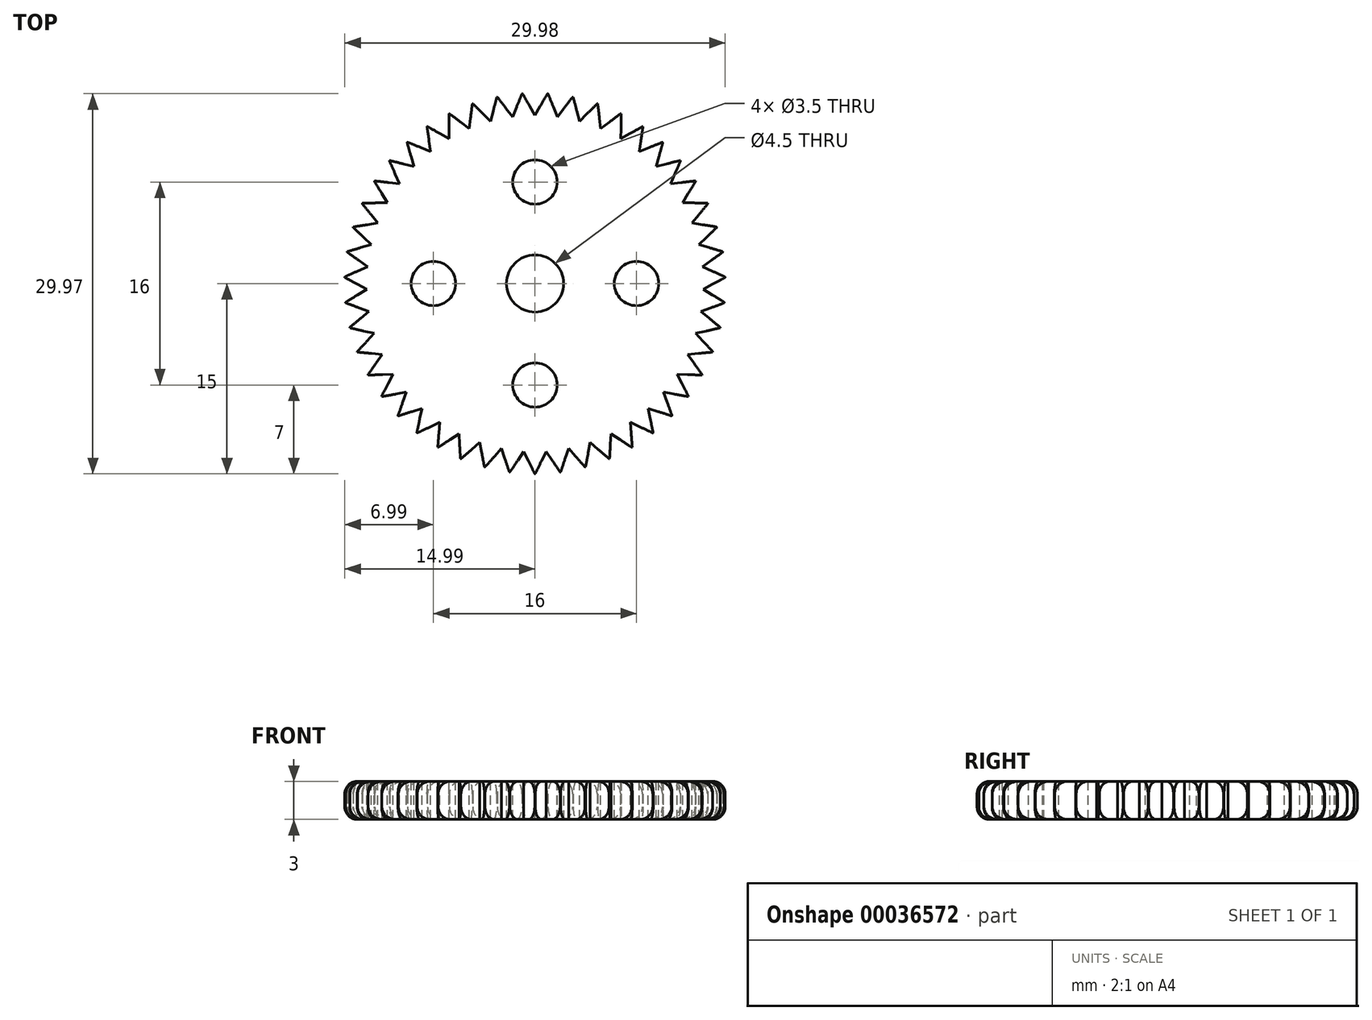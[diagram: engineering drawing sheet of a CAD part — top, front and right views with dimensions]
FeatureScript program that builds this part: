
annotation { "Feature Type Name" : "Feature", "Feature Type Description" : "" }
export const myFeature = defineFeature(function(context is Context, id is Id, definition is map)
    precondition{}
    {
        {
            var Q0;
            Q0=qCreatedBy(makeId("Top.planeOp"),FACE);
            var sketch = newSketch(context, id + "F0", { "sketchPlane" : qUnion([Q0])});
            skCircle(sketch, "E0", {"center": v(0, 0) * mm, "radius": 15 * mm});
            skCircle(sketch, "E1", {"center": v(0, 0) * mm, "radius": 2.25 * mm});
            skSolve(sketch);
        }
        {
            var Q0;
            Q0 = qSketchRegion(id + "F0", true);
            extrude(context, id + "F1", {"entities" : qUnion([Q0]), "depth" : 3 * mm});
        }
        {
            var Q0;
            Q0=makeQuery(id+"F1.opExtrude","CAP_EDGE",EDGE,{"disambiguationData":[OSD([sQuery(id+"F0.wireOp",EDGE,"E0")])],"isStart":false});
            var Q1;
            Q1=makeQuery(id+"F1.opExtrude","CAP_EDGE",EDGE,{"disambiguationData":[OSD([sQuery(id+"F0.wireOp",EDGE,"E0")])],"isStart":true});
            fillet(context, id + "F2", {"entities" : qUnion([Q0, Q1]), "radius" : 1 * mm, "tangentPropagation" : true, "allowEdgeOverflow" : false});
        }
        {
            var Q0;
            Q0=makeQuery(id+"F1.opExtrude","CAP_FACE",FACE,{"disambiguationData":[OSD([sQuery(id+"F0.wireOp",EDGE,"E0"),sQuery(id+"F0.wireOp",EDGE,"E1")])],"isStart":false});
            var sketch = newSketch(context, id + "F3", { "sketchPlane" : qUnion([Q0])});
            skCircle(sketch, "E2.cCircle", {"center": v(0, 14.42) * mm, "radius": 0.58 * mm, "construction": true});
            skLineSegment(sketch, "E2.0", {"start": v(1, 15) * mm, "end": v(0, 13.27) * mm});
            skLineSegment(sketch, "E2.1", {"start": v(0, 13.27) * mm, "end": v(-1, 15) * mm});
            skLineSegment(sketch, "E2.2", {"start": v(-1, 15) * mm, "end": v(1, 15) * mm});
            skPoint(sketch, "E3", {"position": v(0, 15) * mm});
            skLineSegment(sketch, "E4.1.0", {"start": v(-1, 15) * mm, "end": v(-1.77, 13.15) * mm});
            skLineSegment(sketch, "E4.1.1", {"start": v(-1.77, 13.15) * mm, "end": v(-3, 14.73) * mm});
            skLineSegment(sketch, "E4.1.2", {"start": v(-3, 14.73) * mm, "end": v(-1, 15) * mm});
            skLineSegment(sketch, "E4.2.0", {"start": v(-3, 14.73) * mm, "end": v(-3.5, 12.8) * mm});
            skLineSegment(sketch, "E4.2.1", {"start": v(-3.5, 12.8) * mm, "end": v(-4.93, 14.2) * mm});
            skLineSegment(sketch, "E4.2.2", {"start": v(-4.93, 14.2) * mm, "end": v(-3, 14.73) * mm});
            skLineSegment(sketch, "E4.3.0", {"start": v(-4.94, 14.2) * mm, "end": v(-5.18, 12.22) * mm});
            skLineSegment(sketch, "E4.3.1", {"start": v(-5.18, 12.22) * mm, "end": v(-6.78, 13.42) * mm});
            skLineSegment(sketch, "E4.3.2", {"start": v(-6.78, 13.42) * mm, "end": v(-4.94, 14.2) * mm});
            skLineSegment(sketch, "E4.4.0", {"start": v(-6.78, 13.42) * mm, "end": v(-6.76, 11.42) * mm});
            skLineSegment(sketch, "E4.4.1", {"start": v(-6.76, 11.42) * mm, "end": v(-8.5, 12.4) * mm});
            skLineSegment(sketch, "E4.4.2", {"start": v(-8.5, 12.4) * mm, "end": v(-6.78, 13.42) * mm});
            skLineSegment(sketch, "E4.5.0", {"start": v(-8.51, 12.4) * mm, "end": v(-8.22, 10.41) * mm});
            skLineSegment(sketch, "E4.5.1", {"start": v(-8.22, 10.41) * mm, "end": v(-10.08, 11.15) * mm});
            skLineSegment(sketch, "E4.5.2", {"start": v(-10.08, 11.15) * mm, "end": v(-8.51, 12.4) * mm});
            skLineSegment(sketch, "E4.6.0", {"start": v(-10.09, 11.15) * mm, "end": v(-9.54, 9.22) * mm});
            skLineSegment(sketch, "E4.6.1", {"start": v(-9.54, 9.22) * mm, "end": v(-11.48, 9.7) * mm});
            skLineSegment(sketch, "E4.6.2", {"start": v(-11.48, 9.7) * mm, "end": v(-10.09, 11.15) * mm});
            skLineSegment(sketch, "E4.7.0", {"start": v(-11.48, 9.7) * mm, "end": v(-10.68, 7.87) * mm});
            skLineSegment(sketch, "E4.7.1", {"start": v(-10.68, 7.87) * mm, "end": v(-12.67, 8.1) * mm});
            skLineSegment(sketch, "E4.7.2", {"start": v(-12.67, 8.1) * mm, "end": v(-11.48, 9.7) * mm});
            skLineSegment(sketch, "E4.8.0", {"start": v(-12.67, 8.09) * mm, "end": v(-11.64, 6.38) * mm});
            skLineSegment(sketch, "E4.8.1", {"start": v(-11.64, 6.38) * mm, "end": v(-13.63, 6.33) * mm});
            skLineSegment(sketch, "E4.8.2", {"start": v(-13.63, 6.33) * mm, "end": v(-12.67, 8.09) * mm});
            skLineSegment(sketch, "E4.9.0", {"start": v(-13.64, 6.32) * mm, "end": v(-12.38, 4.77) * mm});
            skLineSegment(sketch, "E4.9.1", {"start": v(-12.38, 4.77) * mm, "end": v(-14.36, 4.46) * mm});
            skLineSegment(sketch, "E4.9.2", {"start": v(-14.36, 4.46) * mm, "end": v(-13.64, 6.32) * mm});
            skLineSegment(sketch, "E4.10.0", {"start": v(-14.36, 4.45) * mm, "end": v(-12.9, 3.08) * mm});
            skLineSegment(sketch, "E4.10.1", {"start": v(-12.9, 3.08) * mm, "end": v(-14.82, 2.5) * mm});
            skLineSegment(sketch, "E4.10.2", {"start": v(-14.82, 2.5) * mm, "end": v(-14.36, 4.45) * mm});
            skLineSegment(sketch, "E4.11.0", {"start": v(-14.82, 2.5) * mm, "end": v(-13.2, 1.33) * mm});
            skLineSegment(sketch, "E4.11.1", {"start": v(-13.2, 1.33) * mm, "end": v(-15.02, 0.5) * mm});
            skLineSegment(sketch, "E4.11.2", {"start": v(-15.02, 0.5) * mm, "end": v(-14.82, 2.5) * mm});
            skLineSegment(sketch, "E4.12.0", {"start": v(-15.03, 0.5) * mm, "end": v(-13.26, -0.44) * mm});
            skLineSegment(sketch, "E4.12.1", {"start": v(-13.26, -0.44) * mm, "end": v(-14.96, -1.5) * mm});
            skLineSegment(sketch, "E4.12.2", {"start": v(-14.96, -1.5) * mm, "end": v(-15.03, 0.5) * mm});
            skLineSegment(sketch, "E4.13.0", {"start": v(-14.96, -1.5) * mm, "end": v(-13.08, -2.2) * mm});
            skLineSegment(sketch, "E4.13.1", {"start": v(-13.08, -2.2) * mm, "end": v(-14.62, -3.48) * mm});
            skLineSegment(sketch, "E4.13.2", {"start": v(-14.62, -3.48) * mm, "end": v(-14.96, -1.5) * mm});
            skLineSegment(sketch, "E4.14.0", {"start": v(-14.62, -3.49) * mm, "end": v(-12.67, -3.93) * mm});
            skLineSegment(sketch, "E4.14.1", {"start": v(-12.67, -3.93) * mm, "end": v(-14.03, -5.4) * mm});
            skLineSegment(sketch, "E4.14.2", {"start": v(-14.03, -5.4) * mm, "end": v(-14.62, -3.49) * mm});
            skLineSegment(sketch, "E4.15.0", {"start": v(-14.03, -5.4) * mm, "end": v(-12.04, -5.58) * mm});
            skLineSegment(sketch, "E4.15.1", {"start": v(-12.04, -5.58) * mm, "end": v(-13.19, -7.22) * mm});
            skLineSegment(sketch, "E4.15.2", {"start": v(-13.19, -7.22) * mm, "end": v(-14.03, -5.4) * mm});
            skLineSegment(sketch, "E4.16.0", {"start": v(-13.18, -7.23) * mm, "end": v(-11.18, -7.14) * mm});
            skLineSegment(sketch, "E4.16.1", {"start": v(-11.18, -7.14) * mm, "end": v(-12.1, -8.91) * mm});
            skLineSegment(sketch, "E4.16.2", {"start": v(-12.1, -8.91) * mm, "end": v(-13.18, -7.23) * mm});
            skLineSegment(sketch, "E4.17.0", {"start": v(-12.1, -8.92) * mm, "end": v(-10.13, -8.57) * mm});
            skLineSegment(sketch, "E4.17.1", {"start": v(-10.13, -8.57) * mm, "end": v(-10.8, -10.45) * mm});
            skLineSegment(sketch, "E4.17.2", {"start": v(-10.8, -10.45) * mm, "end": v(-12.1, -8.92) * mm});
            skLineSegment(sketch, "E4.18.0", {"start": v(-10.8, -10.45) * mm, "end": v(-8.9, -9.84) * mm});
            skLineSegment(sketch, "E4.18.1", {"start": v(-8.9, -9.84) * mm, "end": v(-9.32, -11.8) * mm});
            skLineSegment(sketch, "E4.18.2", {"start": v(-9.32, -11.8) * mm, "end": v(-10.8, -10.45) * mm});
            skLineSegment(sketch, "E4.19.0", {"start": v(-9.31, -11.8) * mm, "end": v(-7.5, -10.94) * mm});
            skLineSegment(sketch, "E4.19.1", {"start": v(-7.5, -10.94) * mm, "end": v(-7.66, -12.93) * mm});
            skLineSegment(sketch, "E4.19.2", {"start": v(-7.66, -12.93) * mm, "end": v(-9.31, -11.8) * mm});
            skLineSegment(sketch, "E4.20.0", {"start": v(-7.66, -12.94) * mm, "end": v(-5.98, -11.84) * mm});
            skLineSegment(sketch, "E4.20.1", {"start": v(-5.98, -11.84) * mm, "end": v(-5.87, -13.84) * mm});
            skLineSegment(sketch, "E4.20.2", {"start": v(-5.87, -13.84) * mm, "end": v(-7.66, -12.94) * mm});
            skLineSegment(sketch, "E4.21.0", {"start": v(-5.87, -13.84) * mm, "end": v(-4.35, -12.53) * mm});
            skLineSegment(sketch, "E4.21.1", {"start": v(-4.35, -12.53) * mm, "end": v(-3.98, -14.5) * mm});
            skLineSegment(sketch, "E4.21.2", {"start": v(-3.98, -14.5) * mm, "end": v(-5.87, -13.84) * mm});
            skLineSegment(sketch, "E4.22.0", {"start": v(-3.97, -14.5) * mm, "end": v(-2.64, -13) * mm});
            skLineSegment(sketch, "E4.22.1", {"start": v(-2.64, -13) * mm, "end": v(-2, -14.9) * mm});
            skLineSegment(sketch, "E4.22.2", {"start": v(-2, -14.9) * mm, "end": v(-3.97, -14.5) * mm});
            skLineSegment(sketch, "E4.23.0", {"start": v(-2, -14.9) * mm, "end": v(-0.89, -13.24) * mm});
            skLineSegment(sketch, "E4.23.1", {"start": v(-0.89, -13.24) * mm, "end": v(0, -15.03) * mm});
            skLineSegment(sketch, "E4.23.2", {"start": v(0, -15.03) * mm, "end": v(-2, -14.9) * mm});
            skLineSegment(sketch, "E4.24.0", {"start": v(0, -15.03) * mm, "end": v(0.89, -13.24) * mm});
            skLineSegment(sketch, "E4.24.1", {"start": v(0.89, -13.24) * mm, "end": v(2, -14.9) * mm});
            skLineSegment(sketch, "E4.24.2", {"start": v(2, -14.9) * mm, "end": v(0, -15.03) * mm});
            skLineSegment(sketch, "E4.25.0", {"start": v(2, -14.9) * mm, "end": v(2.64, -13) * mm});
            skLineSegment(sketch, "E4.25.1", {"start": v(2.64, -13) * mm, "end": v(3.97, -14.5) * mm});
            skLineSegment(sketch, "E4.25.2", {"start": v(3.97, -14.5) * mm, "end": v(2, -14.9) * mm});
            skLineSegment(sketch, "E4.26.0", {"start": v(3.98, -14.5) * mm, "end": v(4.35, -12.53) * mm});
            skLineSegment(sketch, "E4.26.1", {"start": v(4.35, -12.53) * mm, "end": v(5.87, -13.84) * mm});
            skLineSegment(sketch, "E4.26.2", {"start": v(5.87, -13.84) * mm, "end": v(3.98, -14.5) * mm});
            skLineSegment(sketch, "E4.27.0", {"start": v(5.87, -13.84) * mm, "end": v(5.98, -11.84) * mm});
            skLineSegment(sketch, "E4.27.1", {"start": v(5.98, -11.84) * mm, "end": v(7.66, -12.94) * mm});
            skLineSegment(sketch, "E4.27.2", {"start": v(7.66, -12.94) * mm, "end": v(5.87, -13.84) * mm});
            skLineSegment(sketch, "E4.28.0", {"start": v(7.66, -12.93) * mm, "end": v(7.5, -10.94) * mm});
            skLineSegment(sketch, "E4.28.1", {"start": v(7.5, -10.94) * mm, "end": v(9.31, -11.8) * mm});
            skLineSegment(sketch, "E4.28.2", {"start": v(9.31, -11.8) * mm, "end": v(7.66, -12.93) * mm});
            skLineSegment(sketch, "E4.29.0", {"start": v(9.32, -11.8) * mm, "end": v(8.9, -9.84) * mm});
            skLineSegment(sketch, "E4.29.1", {"start": v(8.9, -9.84) * mm, "end": v(10.8, -10.45) * mm});
            skLineSegment(sketch, "E4.29.2", {"start": v(10.8, -10.45) * mm, "end": v(9.32, -11.8) * mm});
            skLineSegment(sketch, "E4.30.0", {"start": v(10.8, -10.45) * mm, "end": v(10.13, -8.57) * mm});
            skLineSegment(sketch, "E4.30.1", {"start": v(10.13, -8.57) * mm, "end": v(12.1, -8.92) * mm});
            skLineSegment(sketch, "E4.30.2", {"start": v(12.1, -8.92) * mm, "end": v(10.8, -10.45) * mm});
            skLineSegment(sketch, "E4.31.0", {"start": v(12.1, -8.91) * mm, "end": v(11.18, -7.14) * mm});
            skLineSegment(sketch, "E4.31.1", {"start": v(11.18, -7.14) * mm, "end": v(13.18, -7.23) * mm});
            skLineSegment(sketch, "E4.31.2", {"start": v(13.18, -7.23) * mm, "end": v(12.1, -8.91) * mm});
            skLineSegment(sketch, "E4.32.0", {"start": v(13.19, -7.22) * mm, "end": v(12.04, -5.58) * mm});
            skLineSegment(sketch, "E4.32.1", {"start": v(12.04, -5.58) * mm, "end": v(14.03, -5.4) * mm});
            skLineSegment(sketch, "E4.32.2", {"start": v(14.03, -5.4) * mm, "end": v(13.19, -7.22) * mm});
            skLineSegment(sketch, "E4.33.0", {"start": v(14.03, -5.4) * mm, "end": v(12.67, -3.93) * mm});
            skLineSegment(sketch, "E4.33.1", {"start": v(12.67, -3.93) * mm, "end": v(14.62, -3.49) * mm});
            skLineSegment(sketch, "E4.33.2", {"start": v(14.62, -3.49) * mm, "end": v(14.03, -5.4) * mm});
            skLineSegment(sketch, "E4.34.0", {"start": v(14.62, -3.48) * mm, "end": v(13.08, -2.2) * mm});
            skLineSegment(sketch, "E4.34.1", {"start": v(13.08, -2.2) * mm, "end": v(14.96, -1.5) * mm});
            skLineSegment(sketch, "E4.34.2", {"start": v(14.96, -1.5) * mm, "end": v(14.62, -3.48) * mm});
            skLineSegment(sketch, "E4.35.0", {"start": v(14.96, -1.5) * mm, "end": v(13.26, -0.44) * mm});
            skLineSegment(sketch, "E4.35.1", {"start": v(13.26, -0.44) * mm, "end": v(15.03, 0.5) * mm});
            skLineSegment(sketch, "E4.35.2", {"start": v(15.03, 0.5) * mm, "end": v(14.96, -1.5) * mm});
            skLineSegment(sketch, "E4.36.0", {"start": v(15.02, 0.5) * mm, "end": v(13.2, 1.33) * mm});
            skLineSegment(sketch, "E4.36.1", {"start": v(13.2, 1.33) * mm, "end": v(14.82, 2.5) * mm});
            skLineSegment(sketch, "E4.36.2", {"start": v(14.82, 2.5) * mm, "end": v(15.02, 0.5) * mm});
            skLineSegment(sketch, "E4.37.0", {"start": v(14.82, 2.5) * mm, "end": v(12.9, 3.08) * mm});
            skLineSegment(sketch, "E4.37.1", {"start": v(12.9, 3.08) * mm, "end": v(14.36, 4.45) * mm});
            skLineSegment(sketch, "E4.37.2", {"start": v(14.36, 4.45) * mm, "end": v(14.82, 2.5) * mm});
            skLineSegment(sketch, "E4.38.0", {"start": v(14.36, 4.46) * mm, "end": v(12.38, 4.77) * mm});
            skLineSegment(sketch, "E4.38.1", {"start": v(12.38, 4.77) * mm, "end": v(13.64, 6.32) * mm});
            skLineSegment(sketch, "E4.38.2", {"start": v(13.64, 6.32) * mm, "end": v(14.36, 4.46) * mm});
            skLineSegment(sketch, "E4.39.0", {"start": v(13.63, 6.33) * mm, "end": v(11.64, 6.38) * mm});
            skLineSegment(sketch, "E4.39.1", {"start": v(11.64, 6.38) * mm, "end": v(12.67, 8.09) * mm});
            skLineSegment(sketch, "E4.39.2", {"start": v(12.67, 8.09) * mm, "end": v(13.63, 6.33) * mm});
            skLineSegment(sketch, "E4.40.0", {"start": v(12.67, 8.1) * mm, "end": v(10.68, 7.87) * mm});
            skLineSegment(sketch, "E4.40.1", {"start": v(10.68, 7.87) * mm, "end": v(11.48, 9.7) * mm});
            skLineSegment(sketch, "E4.40.2", {"start": v(11.48, 9.7) * mm, "end": v(12.67, 8.1) * mm});
            skLineSegment(sketch, "E4.41.0", {"start": v(11.48, 9.7) * mm, "end": v(9.54, 9.22) * mm});
            skLineSegment(sketch, "E4.41.1", {"start": v(9.54, 9.22) * mm, "end": v(10.09, 11.15) * mm});
            skLineSegment(sketch, "E4.41.2", {"start": v(10.09, 11.15) * mm, "end": v(11.48, 9.7) * mm});
            skLineSegment(sketch, "E4.42.0", {"start": v(10.08, 11.15) * mm, "end": v(8.22, 10.41) * mm});
            skLineSegment(sketch, "E4.42.1", {"start": v(8.22, 10.41) * mm, "end": v(8.51, 12.4) * mm});
            skLineSegment(sketch, "E4.42.2", {"start": v(8.51, 12.4) * mm, "end": v(10.08, 11.15) * mm});
            skLineSegment(sketch, "E4.43.0", {"start": v(8.5, 12.4) * mm, "end": v(6.76, 11.42) * mm});
            skLineSegment(sketch, "E4.43.1", {"start": v(6.76, 11.42) * mm, "end": v(6.78, 13.42) * mm});
            skLineSegment(sketch, "E4.43.2", {"start": v(6.78, 13.42) * mm, "end": v(8.5, 12.4) * mm});
            skLineSegment(sketch, "E4.44.0", {"start": v(6.78, 13.42) * mm, "end": v(5.18, 12.22) * mm});
            skLineSegment(sketch, "E4.44.1", {"start": v(5.18, 12.22) * mm, "end": v(4.94, 14.2) * mm});
            skLineSegment(sketch, "E4.44.2", {"start": v(4.94, 14.2) * mm, "end": v(6.78, 13.42) * mm});
            skLineSegment(sketch, "E4.45.0", {"start": v(4.93, 14.2) * mm, "end": v(3.5, 12.8) * mm});
            skLineSegment(sketch, "E4.45.1", {"start": v(3.5, 12.8) * mm, "end": v(3, 14.73) * mm});
            skLineSegment(sketch, "E4.45.2", {"start": v(3, 14.73) * mm, "end": v(4.93, 14.2) * mm});
            skLineSegment(sketch, "E4.46.0", {"start": v(3, 14.73) * mm, "end": v(1.77, 13.15) * mm});
            skLineSegment(sketch, "E4.46.1", {"start": v(1.77, 13.15) * mm, "end": v(1, 15) * mm});
            skLineSegment(sketch, "E4.46.2", {"start": v(1, 15) * mm, "end": v(3, 14.73) * mm});
            skPoint(sketch, "E4.center", {"position": v(0, 0) * mm});
            skSolve(sketch);
        }
        {
            var Q0;
            Q0 = qSketchRegion(id + "F3", true);
            extrude(context, id + "F4", {"entities" : qUnion([Q0]), "operationType" : NewBodyOperationType.REMOVE, "endBound" : BoundingType.THROUGH_ALL, "oppositeDirection" : true, "depth" : 25 * mm});
        }
        {
            var Q0;
            Q0=makeQuery(id+"F1.opExtrude","CAP_FACE",FACE,{"disambiguationData":[OSD([sQuery(id+"F0.wireOp",EDGE,"E0"),sQuery(id+"F0.wireOp",EDGE,"E1")])],"isStart":false});
            var sketch = newSketch(context, id + "F5", { "sketchPlane" : qUnion([Q0])});
            skCircle(sketch, "E5", {"center": v(0, 8) * mm, "radius": 1.75 * mm});
            skCircle(sketch, "E6.1.0", {"center": v(-8, 0) * mm, "radius": 1.75 * mm});
            skCircle(sketch, "E6.2.0", {"center": v(0, -8) * mm, "radius": 1.75 * mm});
            skCircle(sketch, "E6.3.0", {"center": v(8, 0) * mm, "radius": 1.75 * mm});
            skPoint(sketch, "E6.center", {"position": v(0, 0) * mm});
            skSolve(sketch);
        }
        {
            var Q0;
            Q0 = qSketchRegion(id + "F5", true);
            extrude(context, id + "F6", {"entities" : qUnion([Q0]), "operationType" : NewBodyOperationType.REMOVE, "endBound" : BoundingType.THROUGH_ALL, "oppositeDirection" : true, "depth" : 25 * mm});
        }
    });
